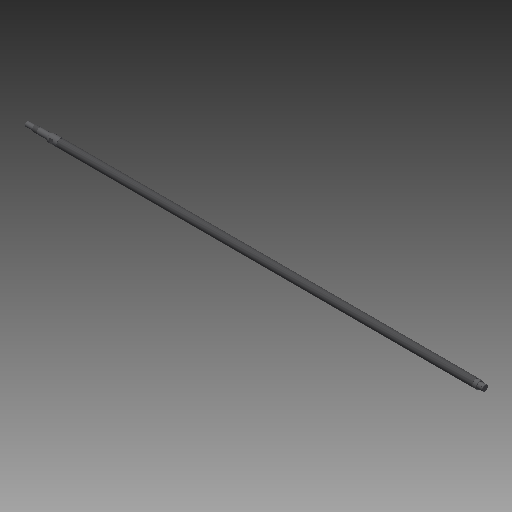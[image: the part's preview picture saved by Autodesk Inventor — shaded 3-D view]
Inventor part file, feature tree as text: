
AUTODESK INVENTOR PART (.ipt)
format: ipt  version: 2018 (Build 220112000, 112)  size: 144,896 bytes
history: native  units: mm
features: other x21, sketch x5, revolve x3, thread x2, extrude x2
ambient origin geometry x8: Origin, YZ Plane, XZ Plane, XY Plane, X Axis, Y Axis, Z Axis, Center Point
bodies: Solid1 (feature_tree)
feature tree (33):
  revolve  "Revolution1"  [1 undecoded]
  thread  "Thread1"  [1 undecoded]
  revolve  "Revolution2"  [1 undecoded]
  thread  "Thread2"  [1 undecoded]
  extrude  "Extrusion1"  TaperAngle=0.0deg  [1 undecoded]
  extrude  "Extrusion2"  [1 undecoded]
  revolve  "Revolution3"  [1 undecoded]
  other  "FSS_XY"
  other  "FSS_YZ"
  other  "FSS_ZX"
  other  "FSS_X"
  other  "FSS_Y"
  other  "FSS_Z"
  other  "FSS_Center"
  other  "SSS_XY"
  other  "SSS_YZ"
  other  "SSS_ZX"
  other  "SSS_X"
  other  "SSS_Y"
  other  "SSS_Z"
  other  "SSS_Center"
  other  "bnt_s_1_XY"
  other  "bnt_s_1_YZ"
  other  "bnt_s_1_ZX"
  other  "bnt_s_1_X"
  other  "bnt_s_1_Y"
  other  "bnt_s_1_Z"
  other  "bnt_s_1_Center"
  sketch  "Sketch_1"  dims[d0=360.0deg d1=1058.0mm d2=0.0mm d3=360.0deg]
  sketch  "Sketch_10"  dims[d4=11.3865mm d5=0.0mm d6=4.0mm d7=0.0mm d8=4.0mm d9=0.0mm]
  sketch  "Sketch_11"  dims[d10=360.0deg d11=0.0mm d12=0.0mm d13=0.0mm]
  sketch  "Sketch_12"
  sketch  "Sketch_16"
note: 7 required parameter values undecoded (feature->parameter linkage not recoverable at this tier; creation-order binding heuristic only, values carry confidence <= 0.55)